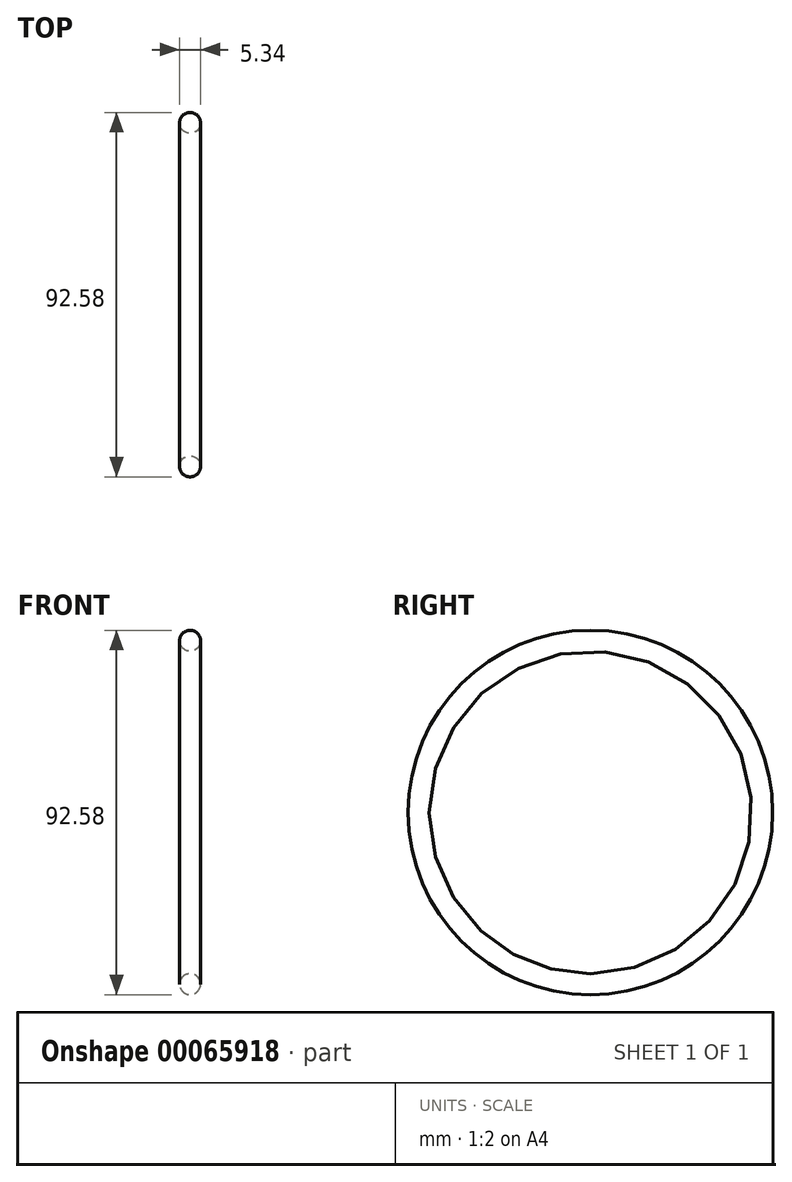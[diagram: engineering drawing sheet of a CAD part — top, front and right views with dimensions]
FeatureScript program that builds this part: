
annotation { "Feature Type Name" : "Feature", "Feature Type Description" : "" }
export const myFeature = defineFeature(function(context is Context, id is Id, definition is map)
    precondition{}
    {
        {
            var Q0;
            Q0=qCreatedBy(makeId("Front.planeOp"),FACE);
            var sketch = newSketch(context, id + "F0", { "sketchPlane" : qUnion([Q0])});
            skLineSegment(sketch, "E0", {"start": v(0, 0) * mm, "end": v(-6.06, 0) * mm, "construction": true});
            skCircle(sketch, "E1", {"center": v(0, 43.62) * mm, "radius": 2.67 * mm});
            skSolve(sketch);
        }
        {
            var Q0;
            Q0=makeQuery(id+"F0.imprint","IMPRINT",FACE,{"disambiguationData":[TD([[makeQuery(id+"F0.imprint","IMPRINT",EDGE,{"derivedFrom":sQuery(id+"F0.wireOp",EDGE,"E1")}),1.0]])]});
            var Q1;
            Q1=sQuery(id+"F0.wireOp",EDGE,"E0");
            revolve(context, id + "F1", {"entities" : qUnion([Q0]), "axis" : qUnion([Q1]), "revolveType" : RevolveType.FULL});
        }
    });
